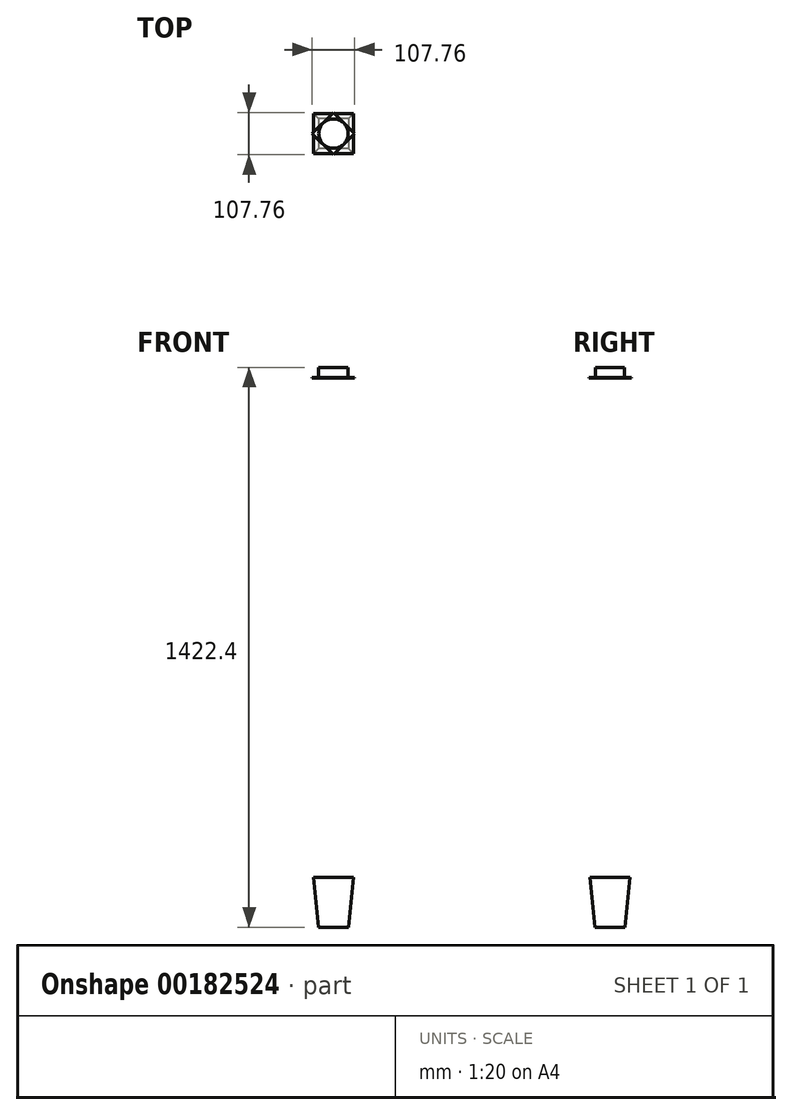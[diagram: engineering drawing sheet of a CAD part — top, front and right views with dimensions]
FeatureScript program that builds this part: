
annotation { "Feature Type Name" : "Feature", "Feature Type Description" : "" }
export const myFeature = defineFeature(function(context is Context, id is Id, definition is map)
    precondition{}
    {
        {
            var Q0;
            Q0=qCreatedBy(makeId("Top.planeOp"),FACE);
            cPlane(context, id + "F0", {"entities" : qUnion([Q0]), "cplaneType" : CPlaneType.OFFSET, "offset" : 127 * mm, "width" : 152.4 * mm, "height" : 152.4 * mm});
        }
        {
            var Q0;
            Q0=qCreatedBy(id+"F0.planeOp",FACE);
            cPlane(context, id + "F1", {"entities" : qUnion([Q0]), "cplaneType" : CPlaneType.OFFSET, "offset" : 1270 * mm, "width" : 152.4 * mm, "height" : 152.4 * mm});
        }
        {
            var Q0;
            Q0=qCreatedBy(makeId("Top.planeOp"),FACE);
            var sketch = newSketch(context, id + "F2", { "sketchPlane" : qUnion([Q0])});
            skLineSegment(sketch, "E0.bottom", {"start": v(38.1, 38.1) * mm, "end": v(-38.1, 38.1) * mm});
            skLineSegment(sketch, "E0.top", {"start": v(38.1, -38.1) * mm, "end": v(-38.1, -38.1) * mm});
            skLineSegment(sketch, "E0.left", {"start": v(38.1, 38.1) * mm, "end": v(38.1, -38.1) * mm});
            skLineSegment(sketch, "E0.right", {"start": v(-38.1, 38.1) * mm, "end": v(-38.1, -38.1) * mm});
            skPoint(sketch, "E0.middle", {"position": v(0, 0) * mm});
            skSolve(sketch);
        }
        {
            var Q0;
            Q0=qCreatedBy(id+"F0.planeOp",FACE);
            var sketch = newSketch(context, id + "F3", { "sketchPlane" : qUnion([Q0])});
            skLineSegment(sketch, "E1.bottom", {"start": v(50.8, 50.8) * mm, "end": v(-50.8, 50.8) * mm});
            skLineSegment(sketch, "E1.top", {"start": v(50.8, -50.8) * mm, "end": v(-50.8, -50.8) * mm});
            skLineSegment(sketch, "E1.left", {"start": v(50.8, 50.8) * mm, "end": v(50.8, -50.8) * mm});
            skLineSegment(sketch, "E1.right", {"start": v(-50.8, 50.8) * mm, "end": v(-50.8, -50.8) * mm});
            skPoint(sketch, "E1.middle", {"position": v(0, 0) * mm});
            skSolve(sketch);
        }
        {
            var Q0;
            Q0=qCreatedBy(id+"F1.planeOp",FACE);
            var sketch = newSketch(context, id + "F4", { "sketchPlane" : qUnion([Q0])});
            skPoint(sketch, "E2", {"position": v(0, 53.88) * mm});
            skPoint(sketch, "E3", {"position": v(53.88, 0) * mm});
            skPoint(sketch, "E4", {"position": v(0, -53.88) * mm});
            skPoint(sketch, "E5", {"position": v(-53.88, 0) * mm});
            skLineSegment(sketch, "E6", {"start": v(-53.88, 0) * mm, "end": v(0, 53.88) * mm});
            skLineSegment(sketch, "E7", {"start": v(53.88, 0) * mm, "end": v(0, -53.88) * mm});
            skLineSegment(sketch, "E8", {"start": v(-53.88, 0) * mm, "end": v(0, -53.88) * mm});
            skLineSegment(sketch, "E9", {"start": v(0, 53.88) * mm, "end": v(53.88, 0) * mm});
            skSolve(sketch);
        }
        {
            var Q0;
            Q0=qCreatedBy(id+"F1.planeOp",FACE);
            var sketch = newSketch(context, id + "F5", { "sketchPlane" : qUnion([Q0])});
            skCircle(sketch, "E10", {"center": v(0, 0) * mm, "radius": 37.33 * mm});
            skSolve(sketch);
        }
        {
            var Q0;
            Q0=sQuery(id+"F4.wireOp",VERTEX,"E4");
            var Q1;
            Q1=sQuery(id+"F3.wireOp",EDGE,"E1.top");
            loft(context, id + "F6", {"bodyType" : ToolBodyType.SURFACE, "wireProfilesArray" : [{ "wireProfileEntities" : qUnion([Q0]) }, { "wireProfileEntities" : qUnion([Q1]) }]});
        }
        {
            var Q0;
            Q0=sQuery(id+"F4.wireOp",EDGE,"E7");
            var Q1;
            Q1=sQuery(id+"F3.wireOp",VERTEX,"E1.left.end");
            loft(context, id + "F7", {"bodyType" : ToolBodyType.SURFACE, "wireProfilesArray" : [{ "wireProfileEntities" : qUnion([Q0]) }, { "wireProfileEntities" : qUnion([Q1]) }]});
        }
        {
            var Q0;
            Q0=sQuery(id+"F4.wireOp",VERTEX,"E3");
            var Q1;
            Q1=sQuery(id+"F3.wireOp",EDGE,"E1.left");
            var Q2;
            Q2=sQuery(id+"F4.wireOp",VERTEX,"E3");
            loft(context, id + "F8", {"bodyType" : ToolBodyType.SURFACE, "sheetProfilesArray" : [{ "sheetProfileEntities" : qUnion([Q0]) }], "wireProfilesArray" : [{ "wireProfileEntities" : qUnion([Q1]) }, { "wireProfileEntities" : qUnion([Q2]) }]});
        }
        {
            var Q0;
            Q0=sQuery(id+"F4.wireOp",EDGE,"E9");
            var Q1;
            Q1=sQuery(id+"F3.wireOp",VERTEX,"E1.left.start");
            loft(context, id + "F9", {"bodyType" : ToolBodyType.SURFACE, "wireProfilesArray" : [{ "wireProfileEntities" : qUnion([Q0]) }, { "wireProfileEntities" : qUnion([Q1]) }]});
        }
        {
            var Q0;
            Q0=sQuery(id+"F3.wireOp",VERTEX,"E1.right.start");
            var Q1;
            Q1=sQuery(id+"F4.wireOp",EDGE,"E6");
            loft(context, id + "F10", {"bodyType" : ToolBodyType.SURFACE, "wireProfilesArray" : [{ "wireProfileEntities" : qUnion([Q0]) }, { "wireProfileEntities" : qUnion([Q1]) }]});
        }
        {
            var Q0;
            Q0=sQuery(id+"F4.wireOp",VERTEX,"E2");
            var Q1;
            Q1=sQuery(id+"F3.wireOp",EDGE,"E1.bottom");
            loft(context, id + "F11", {"bodyType" : ToolBodyType.SURFACE, "wireProfilesArray" : [{ "wireProfileEntities" : qUnion([Q0]) }, { "wireProfileEntities" : qUnion([Q1]) }]});
        }
        {
            var Q0;
            Q0=sQuery(id+"F3.wireOp",EDGE,"E1.right");
            var Q1;
            Q1=sQuery(id+"F4.wireOp",VERTEX,"E5");
            loft(context, id + "F12", {"bodyType" : ToolBodyType.SURFACE, "wireProfilesArray" : [{ "wireProfileEntities" : qUnion([Q0]) }, { "wireProfileEntities" : qUnion([Q1]) }]});
        }
        {
            var Q0;
            Q0=sQuery(id+"F3.wireOp",VERTEX,"E1.right.end");
            var Q1;
            Q1=sQuery(id+"F4.wireOp",EDGE,"E8");
            loft(context, id + "F13", {"bodyType" : ToolBodyType.SURFACE, "wireProfilesArray" : [{ "wireProfileEntities" : qUnion([Q0]) }, { "wireProfileEntities" : qUnion([Q1]) }]});
        }
        {
            var Q0;
            Q0=makeQuery(id+"F2.imprint","IMPRINT",FACE,{"disambiguationData":[TD([[makeQuery(id+"F2.imprint","IMPRINT",EDGE,{"derivedFrom":sQuery(id+"F2.wireOp",EDGE,"E0.bottom")}),1.0]])]});
            var Q1;
            Q1=makeQuery(id+"F3.imprint","IMPRINT",FACE,{"disambiguationData":[TD([[makeQuery(id+"F3.imprint","IMPRINT",EDGE,{"derivedFrom":sQuery(id+"F3.wireOp",EDGE,"E1.bottom")}),1.0]])]});
            var Q2;
            Q2=sQuery(id+"F3.wireOp",EDGE,"E1.top");
            loft(context, id + "F14", {"sheetProfilesArray" : [{ "sheetProfileEntities" : qUnion([Q0]) }, { "sheetProfileEntities" : qUnion([Q1]) }], "wireProfilesArray" : [{ "wireProfileEntities" : qUnion([Q2]) }]});
        }
        {
            var Q0;
            Q0=makeQuery(id+"F4.imprint","IMPRINT",FACE,{"disambiguationData":[TD([[makeQuery(id+"F4.imprint","IMPRINT",EDGE,{"derivedFrom":sQuery(id+"F4.wireOp",EDGE,"E6")}),-1.0]])]});
            extrude(context, id + "F15", {"entities" : qUnion([Q0]), "oppositeDirection" : true, "depth" : 1.61 * mm});
        }
        {
            var Q0;
            Q0=makeQuery(id+"F5.imprint","IMPRINT",FACE,{"disambiguationData":[TD([[makeQuery(id+"F5.imprint","IMPRINT",EDGE,{"derivedFrom":sQuery(id+"F5.wireOp",EDGE,"E10")}),1.0]])]});
            extrude(context, id + "F16", {"entities" : qUnion([Q0]), "operationType" : NewBodyOperationType.ADD, "depth" : 25.4 * mm});
        }
    });
